# Revit family: IS_PrivoII_T2617_BIM_DE
name_source: partatom
category: Plumbing Fixtures
revit_build: Autodesk Revit MEP 2016 (Build: 20161004_0715(x64)
units: mm (PartAtom-declared; Revit-internal decimal feet)

## family parameters
Always vertical = No
Cut with Voids When Loaded = No
OmniClass Number = 23.45.05.21.11.21
OmniClass Title = Urinals
Part Type = Normal
Room Calculation Point = No
Round Connector Dimension = Use Diameter
Shared = No
Work Plane-Based = No

## types (1)
- T261701 - PRIVO II urinal cover
    Accessories = www.idealstandard.de\ersatzteile
    AssetType = Fixed
    BIMObjectName = ISI_IdealStandard_Wall-HungUrinals_PrivoII_T261701
    BIMobject category = Urinals
    BOSUseNativeGeometries = 1
    BarCode = 8014140410966
    Brand = Ideal Standard
    Brand url = http://www.idealstandard.de
    CodePerformance = 0
    Color = White
    ConnectionType = Plumbing
    Cost = 0 $
    CurrencyUnit = €
    CurrentRevision = 1
    Date of publishing = 20/12/2017
    Description = IS Urinaldeckel PRIVO II, 300x370mm, Weiß
    DurationUnit = Year
    EAN code = https://8014140410966
    Edition number = 1
    ExpectedLife = 25
    Features = IS Urinaldeckel PRIVO II, 300x370mm, Weiß
    Finish = White
    IFC Classification = Sanitary Terminal
    IfcExportAs = IfcSanitaryTerminalType
    Installation instructions = http://www.idealstandard.de
    InstallationInstructions = www.idealstandard.de\produkte
    MainColor = White
    MaintenanceInformation = www.idealstandard.de\produkte
    Manufacturer name = Ideal Standard
    ManufacturerURL = http://www.idealstandard.de
    Material = Duroplast
    Material main = Ceramics
    Model = T261701
    ModelNumber = T261701
    ModelReference = IS Urinaldeckel PRIVO II, 300x370mm, Weiß
    NBS Reference Code = 35-93-82
    NBS Reference Description = Wall-Hung Urinals
    Name = Wall-HungUrinals_PrivoII_T261701
    NettWeight = 1 Kg
    Nominal height = 0
    Nominal width = 0
    NominalDepth = 237 mm  [stored 0.777559 ft]
    NominalHeight = 296 mm
    NominalLength = 237 mm  [stored 0.777559 ft]
    NominalWidth = 301 mm
    OmniClass Code = 23-31 21 00
    OmniClass Description = Urinals
    Product Guid = 20859307-a7a5-4c79-9560-801c2baf9248
    Product SKU = T2617
    Product data url = https://bimobject.com
    Product family = Sanitary
    Product group = Urinal
    Product name = PRIVO II urinal cover
    Product url = http://www.idealstandard.de
    ProductInformation = www.idealstandard.de/produkte
    QR code = http://bimobject.com
    Shape = Sculptured
    Size = 296 x 237 x 301mm
    Space = Internal
    SpareParts = www.idealstandard.de/ersatzteile
    Technical description = http://www.idealstandard.de
    URL = http://www.idealstandard.de
    Uniclass 1.4 Code = L7217
    Uniclass 1.4 Description = Urinals
    Uniclass 2.0 Code = PR-35-93-82
    Uniclass 2.0 Description = Wall-Hung Urinals
    Uniclass 2015 Code = Pr_40_20_93_82
    Uniclass 2015 Name = Wall-hung urinals
    Uniclass2015Code = Pr_40_20_93_82
    Uniclass2015Title = Wall-hung urinals
    Uniclass2015Version = Products v1.1
    UrinalColor = White
    UrinalMaterial = Ceramic
    UrinalType = Wall hung
    Version = 1
    VolumeUnits = Litres
    Weight Net (Kg) = 1

note: [stored X ft] marks values corroborated as IEEE doubles in the binary element streams (Revit-internal decimal feet)

## geometry (parser evidence)
native form markers: Blend x4, Sweep x1
no freeform markers — native parametric forms only
